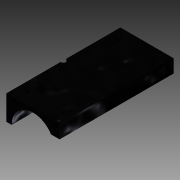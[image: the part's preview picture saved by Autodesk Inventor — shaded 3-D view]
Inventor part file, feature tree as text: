
AUTODESK INVENTOR PART (.ipt)
format: ipt  version: 2015 (Build 190159000, 159)  size: 194,560 bytes
history: native  units: mm
features: other x4, extrude x4, sketch x4, projected_geometry x3
ambient origin geometry x8: Origin, YZ Plane, XZ Plane, XY Plane, X Axis, Y Axis, Z Axis, Center Point
bodies: Solid1 (feature_tree)
feature tree (15):
  other  "motor mount.ipt"
  extrude  "Extrusion1"  Depth=10.0mm
  extrude  "Extrusion2"  Depth=60.0mm
  extrude  "Extrusion4"  Depth=2.3mm
  extrude  "Extrusion5"  Depth=3.0mm
  other  "TaggingFeature1"
  sketch  "Sketch2"  dims[d1=10.0mm d2=11.25mm]
  sketch  "Sketch3"  dims[d3=60.0mm d4=0.0mm d5=2.3mm]
  projected_geometry  "Projected Loop1"
  sketch  "Sketch4"  dims[d6=2.3mm d7=2.3mm]
  projected_geometry  "Projected Loop2"
  sketch  "Sketch5"  dims[d8=2.3mm d9=4.5mm d10=4.5mm d11=6.0mm d12=6.0mm d13=60.0mm d14=0.0mm d15=19.0mm d16=48.0mm d19=6.0mm d20=0.0mm d21=3.0mm d22=100.0mm d23=0.0mm]
  projected_geometry  "Projected Loop3"
  other  "Solid1::motor mount.ipt"
  other  "Srf1"
